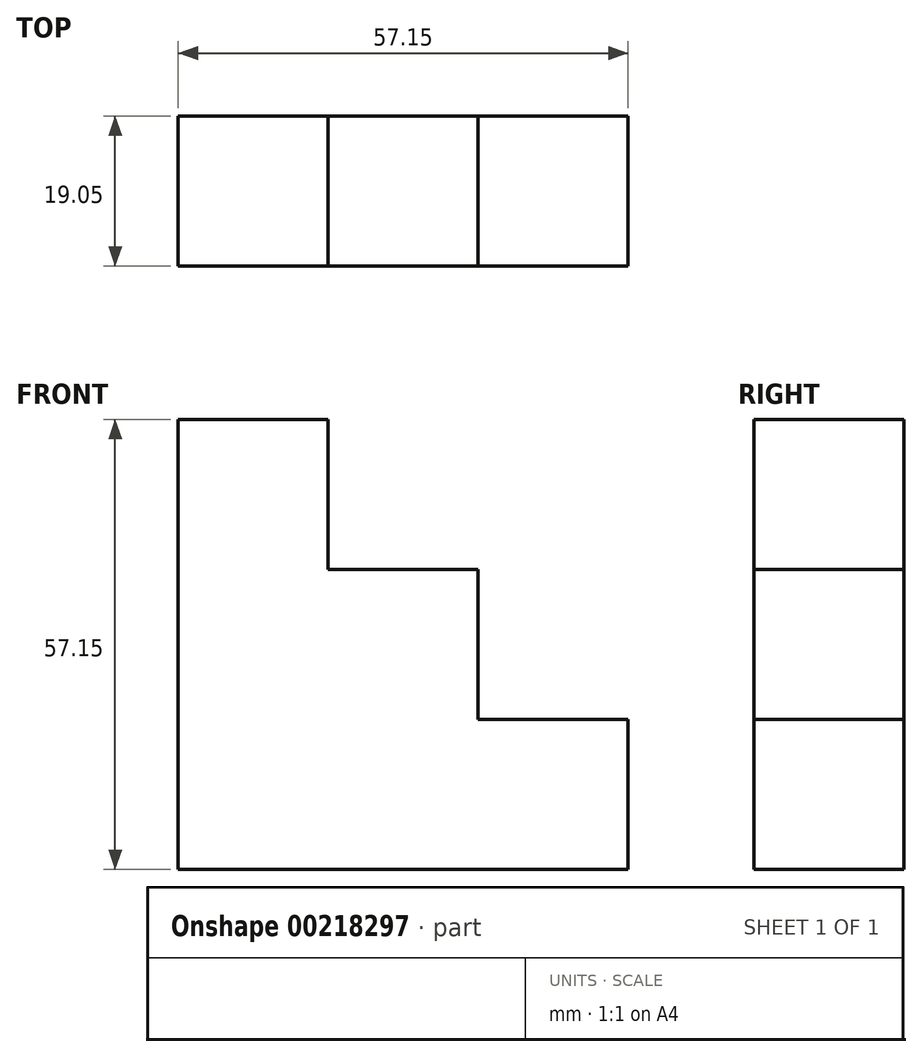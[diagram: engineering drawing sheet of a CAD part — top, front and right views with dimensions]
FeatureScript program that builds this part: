
annotation { "Feature Type Name" : "Feature", "Feature Type Description" : "" }
export const myFeature = defineFeature(function(context is Context, id is Id, definition is map)
    precondition{}
    {
        {
            var Q0;
            Q0=qCreatedBy(makeId("Front.planeOp"),FACE);
            var sketch = newSketch(context, id + "F0", { "sketchPlane" : qUnion([Q0])});
            skLineSegment(sketch, "E0", {"start": v(-64.24, 47.93) * mm, "end": v(-45.2, 47.93) * mm});
            skLineSegment(sketch, "E1", {"start": v(-45.2, 47.93) * mm, "end": v(-45.2, 28.88) * mm});
            skLineSegment(sketch, "E2", {"start": v(-45.2, 28.88) * mm, "end": v(-26.14, 28.88) * mm});
            skLineSegment(sketch, "E3", {"start": v(-26.14, 28.88) * mm, "end": v(-26.14, 9.83) * mm});
            skLineSegment(sketch, "E4", {"start": v(-26.14, 9.83) * mm, "end": v(-7.1, 9.83) * mm});
            skLineSegment(sketch, "E5", {"start": v(-7.1, 9.83) * mm, "end": v(-7.1, -9.22) * mm});
            skLineSegment(sketch, "E6", {"start": v(-7.1, -9.22) * mm, "end": v(-64.24, -9.22) * mm});
            skLineSegment(sketch, "E7", {"start": v(-64.24, -9.22) * mm, "end": v(-64.24, 47.93) * mm});
            skSolve(sketch);
        }
        {
            var Q0;
            Q0=makeQuery(id+"F0.imprint","IMPRINT",FACE,{"disambiguationData":[TD([[makeQuery(id+"F0.imprint","IMPRINT",EDGE,{"derivedFrom":sQuery(id+"F0.wireOp",EDGE,"E0")}),-1.0]])]});
            extrude(context, id + "F1", {"entities" : qUnion([Q0]), "depth" : 19.05 * mm});
        }
    });
